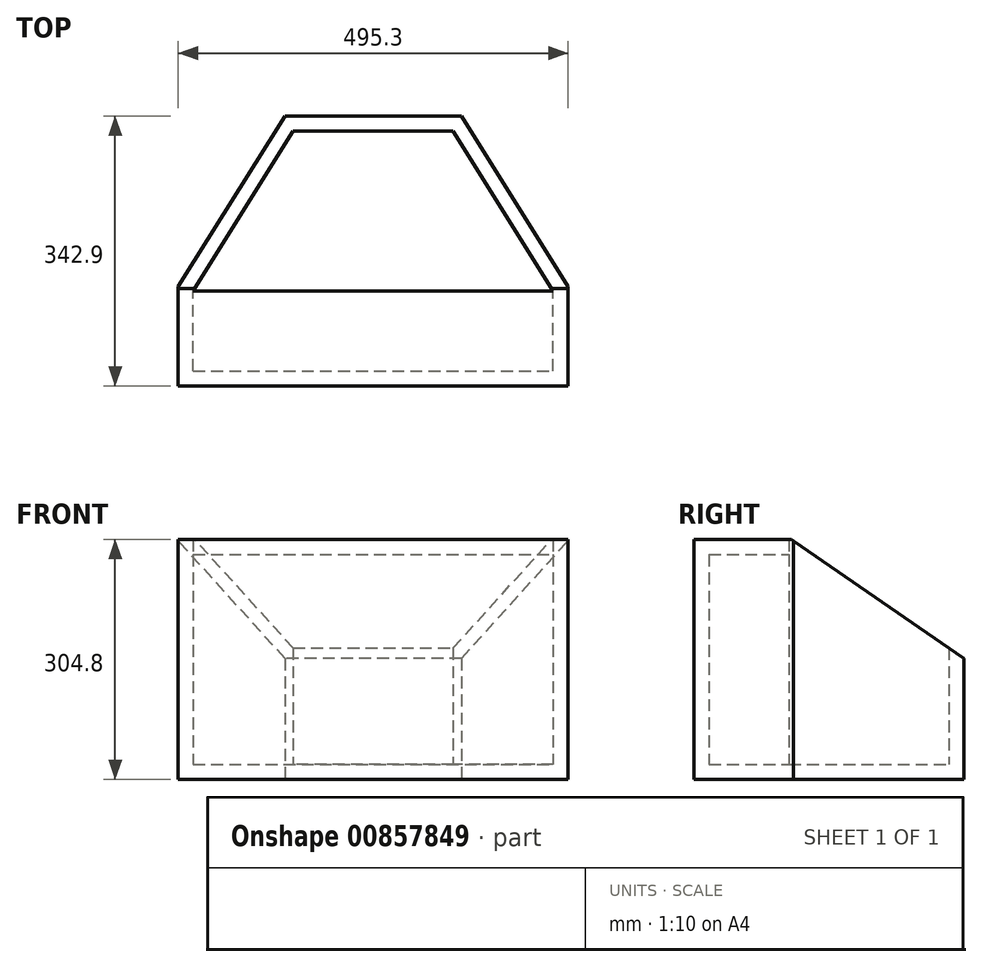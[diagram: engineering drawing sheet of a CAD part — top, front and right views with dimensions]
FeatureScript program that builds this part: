
annotation { "Feature Type Name" : "Feature", "Feature Type Description" : "" }
export const myFeature = defineFeature(function(context is Context, id is Id, definition is map)
    precondition{}
    {
        {
            var Q0;
            Q0=qCreatedBy(makeId("Top.planeOp"),FACE);
            var sketch = newSketch(context, id + "F0", { "sketchPlane" : qUnion([Q0])});
            skLineSegment(sketch, "E0", {"start": v(-228.6, -117.5) * mm, "end": v(228.6, -117.5) * mm});
            skLineSegment(sketch, "E1", {"start": v(228.6, -117.5) * mm, "end": v(228.6, -15.9) * mm});
            skLineSegment(sketch, "E2", {"start": v(228.6, -15.9) * mm, "end": v(101.6, 187.3) * mm});
            skLineSegment(sketch, "E3", {"start": v(101.6, 187.3) * mm, "end": v(-101.6, 187.3) * mm});
            skLineSegment(sketch, "E4.MirrorCS", {"start": v(-228.6, -117.5) * mm, "end": v(-228.6, -15.9) * mm});
            skLineSegment(sketch, "E5.MirrorCS", {"start": v(-228.6, -15.9) * mm, "end": v(-101.6, 187.3) * mm});
            skLineSegment(sketch, "E6", {"start": v(-247.65, -10.44) * mm, "end": v(-112.16, 206.35) * mm});
            skLineSegment(sketch, "E7", {"start": v(-112.16, 206.35) * mm, "end": v(112.2, 206.35) * mm});
            skLineSegment(sketch, "E8", {"start": v(-247.65, -10.44) * mm, "end": v(-247.65, -136.55) * mm});
            skLineSegment(sketch, "E9", {"start": v(-247.65, -136.55) * mm, "end": v(247.65, -136.55) * mm});
            skLineSegment(sketch, "E10.MirrorCS", {"start": v(247.65, -10.44) * mm, "end": v(247.65, -136.55) * mm});
            skLineSegment(sketch, "E11.MirrorCS", {"start": v(247.65, -10.44) * mm, "end": v(112.16, 206.35) * mm});
            skLineSegment(sketch, "E12", {"start": v(-101.6, 187.3) * mm, "end": v(-112.16, 206.35) * mm});
            skLineSegment(sketch, "E13", {"start": v(-228.6, -15.9) * mm, "end": v(-247.65, -10.44) * mm});
            skLineSegment(sketch, "E14", {"start": v(-228.6, -117.5) * mm, "end": v(-247.65, -136.55) * mm});
            skLineSegment(sketch, "E15", {"start": v(247.65, -136.55) * mm, "end": v(228.6, -117.5) * mm});
            skLineSegment(sketch, "E16", {"start": v(228.6, -15.9) * mm, "end": v(247.65, -10.44) * mm});
            skLineSegment(sketch, "E17", {"start": v(101.6, 187.3) * mm, "end": v(112.2, 206.35) * mm});
            skSolve(sketch);
        }
        {
            var Q0;
            {var subQ1=sQuery(id+"F0.wireOp",EDGE,"E3");Q0=makeQuery(id+"F0.imprint","IMPRINT",FACE,{"disambiguationData":[TD([[makeQuery(id+"F0.imprint","IMPRINT",EDGE,{"derivedFrom":subQ1}),-1.0]])]});}
            extrude(context, id + "F1", {"entities" : qUnion([Q0]), "depth" : 177.8 * mm, "offsetDistance" : 25.4 * mm});
        }
        {
            var Q0;
            Q0=makeQuery(id+"F0.imprint","IMPRINT",FACE,{"disambiguationData":[TD([[makeQuery(id+"F0.imprint","IMPRINT",EDGE,{"derivedFrom":sQuery(id+"F0.wireOp",EDGE,"E5.MirrorCS")}),1.0]])]});
            extrude(context, id + "F2", {"entities" : qUnion([Q0]), "operationType" : NewBodyOperationType.ADD, "depth" : 304.8 * mm, "offsetDistance" : 25.4 * mm});
        }
        {
            var Q0;
            {var subQ0=sQuery(id+"F0.wireOp",EDGE,"E2");Q0=makeQuery(id+"F0.imprint","IMPRINT",FACE,{"disambiguationData":[TD([[makeQuery(id+"F0.imprint","IMPRINT",EDGE,{"derivedFrom":subQ0}),-1.0]])]});}
            extrude(context, id + "F3", {"entities" : qUnion([Q0]), "operationType" : NewBodyOperationType.ADD, "depth" : 304.8 * mm, "offsetDistance" : 25.4 * mm});
        }
        {
            var Q0;
            Q0=makeQuery(id+"F0.imprint","IMPRINT",FACE,{"disambiguationData":[TD([[makeQuery(id+"F0.imprint","IMPRINT",EDGE,{"derivedFrom":sQuery(id+"F0.wireOp",EDGE,"E4.MirrorCS")}),1.0]])]});
            extrude(context, id + "F4", {"entities" : qUnion([Q0]), "operationType" : NewBodyOperationType.ADD, "depth" : 304.8 * mm, "offsetDistance" : 25.4 * mm});
        }
        {
            var Q0;
            Q0=makeQuery(id+"F0.imprint","IMPRINT",FACE,{"disambiguationData":[TD([[makeQuery(id+"F0.imprint","IMPRINT",EDGE,{"derivedFrom":sQuery(id+"F0.wireOp",EDGE,"E1")}),-1.0]])]});
            extrude(context, id + "F5", {"entities" : qUnion([Q0]), "operationType" : NewBodyOperationType.ADD, "depth" : 304.8 * mm, "offsetDistance" : 25.4 * mm});
        }
        {
            var Q0;
            Q0=makeQuery(id+"F0.imprint","IMPRINT",FACE,{"disambiguationData":[TD([[makeQuery(id+"F0.imprint","IMPRINT",EDGE,{"derivedFrom":sQuery(id+"F0.wireOp",EDGE,"E0")}),-1.0]])]});
            extrude(context, id + "F6", {"entities" : qUnion([Q0]), "operationType" : NewBodyOperationType.ADD, "depth" : 304.8 * mm, "offsetDistance" : 25.4 * mm});
        }
        {
            var Q0;
            Q0=makeQuery(id+"F0.imprint","IMPRINT",FACE,{"disambiguationData":[TD([[makeQuery(id+"F0.imprint","IMPRINT",EDGE,{"derivedFrom":sQuery(id+"F0.wireOp",EDGE,"E0")}),1.0]])]});
            extrude(context, id + "F7", {"entities" : qUnion([Q0]), "operationType" : NewBodyOperationType.ADD, "depth" : 19.05 * mm, "offsetDistance" : 25.4 * mm});
        }
        {
            var Q0;
            Q0=qCreatedBy(makeId("Right.planeOp"),FACE);
            var sketch = newSketch(context, id + "F8", { "sketchPlane" : qUnion([Q0])});
            skLineSegment(sketch, "E18", {"start": v(-12.7, 304.8) * mm, "end": v(208.28, 152.4) * mm});
            skLineSegment(sketch, "E19", {"start": v(208.28, 152.4) * mm, "end": v(208.28, 311.54) * mm});
            skLineSegment(sketch, "E20", {"start": v(208.28, 311.54) * mm, "end": v(-12.7, 311.54) * mm});
            skLineSegment(sketch, "E21", {"start": v(-12.7, 311.54) * mm, "end": v(-12.7, 304.8) * mm});
            skSolve(sketch);
        }
        {
            var Q0;
            Q0 = qSketchRegion(id + "F8", true);
            extrude(context, id + "F9", {"entities" : qUnion([Q0]), "operationType" : NewBodyOperationType.REMOVE, "endBound" : BoundingType.SYMMETRIC, "oppositeDirection" : true, "depth" : 609.6 * mm, "offsetDistance" : 25.4 * mm});
        }
        {
            var Q0;
            {var subQ0=sQuery(id+"F0.wireOp",EDGE,"E15");var subQ1=sQuery(id+"F0.wireOp",EDGE,"E14");var subQ2=sQuery(id+"F0.wireOp",EDGE,"E16");var subQ3=sQuery(id+"F0.wireOp",EDGE,"E13");Q0=makeQuery(id+"F6.boolean.opBoolean","MERGE",FACE,{"derivedFrom":[makeQuery(id+"F4.boolean.opBoolean","MERGE",FACE,{"derivedFrom":[makeQuery(id+"F2.opExtrude","CAP_FACE",FACE,{"disambiguationData":[OSD([sQuery(id+"F0.wireOp",EDGE,"E5.MirrorCS"),sQuery(id+"F0.wireOp",EDGE,"E6"),sQuery(id+"F0.wireOp",EDGE,"E12"),subQ3])],"isStart":false}),makeQuery(id+"F4.opExtrude","CAP_FACE",FACE,{"disambiguationData":[OSD([sQuery(id+"F0.wireOp",EDGE,"E4.MirrorCS"),sQuery(id+"F0.wireOp",EDGE,"E8"),subQ3,subQ1])],"isStart":false})]}),makeQuery(id+"F5.boolean.opBoolean","MERGE",FACE,{"derivedFrom":[makeQuery(id+"F3.opExtrude","CAP_FACE",FACE,{"disambiguationData":[OSD([sQuery(id+"F0.wireOp",EDGE,"E2"),sQuery(id+"F0.wireOp",EDGE,"E11.MirrorCS"),subQ2,sQuery(id+"F0.wireOp",EDGE,"E17")])],"isStart":false}),makeQuery(id+"F5.opExtrude","CAP_FACE",FACE,{"disambiguationData":[OSD([sQuery(id+"F0.wireOp",EDGE,"E1"),sQuery(id+"F0.wireOp",EDGE,"E10.MirrorCS"),subQ0,subQ2])],"isStart":false})]}),makeQuery(id+"F6.opExtrude","CAP_FACE",FACE,{"disambiguationData":[OSD([sQuery(id+"F0.wireOp",EDGE,"E0"),sQuery(id+"F0.wireOp",EDGE,"E9"),subQ1,subQ0])],"isStart":false})]});}
            var sketch = newSketch(context, id + "F10", { "sketchPlane" : qUnion([Q0])});
            skLineSegment(sketch, "E22.bottom", {"start": v(-247.65, -15.9) * mm, "end": v(247.65, -15.9) * mm});
            skLineSegment(sketch, "E22.top", {"start": v(-247.65, -136.55) * mm, "end": v(247.65, -136.55) * mm});
            skLineSegment(sketch, "E22.left", {"start": v(-247.65, -15.9) * mm, "end": v(-247.65, -136.55) * mm});
            skLineSegment(sketch, "E22.right", {"start": v(247.65, -15.9) * mm, "end": v(247.65, -136.55) * mm});
            skSolve(sketch);
        }
        {
            var Q0;
            Q0 = qSketchRegion(id + "F10", true);
            extrude(context, id + "F11", {"entities" : qUnion([Q0]), "operationType" : NewBodyOperationType.ADD, "oppositeDirection" : true, "depth" : 19.05 * mm, "offsetDistance" : 25.4 * mm});
        }
    });
